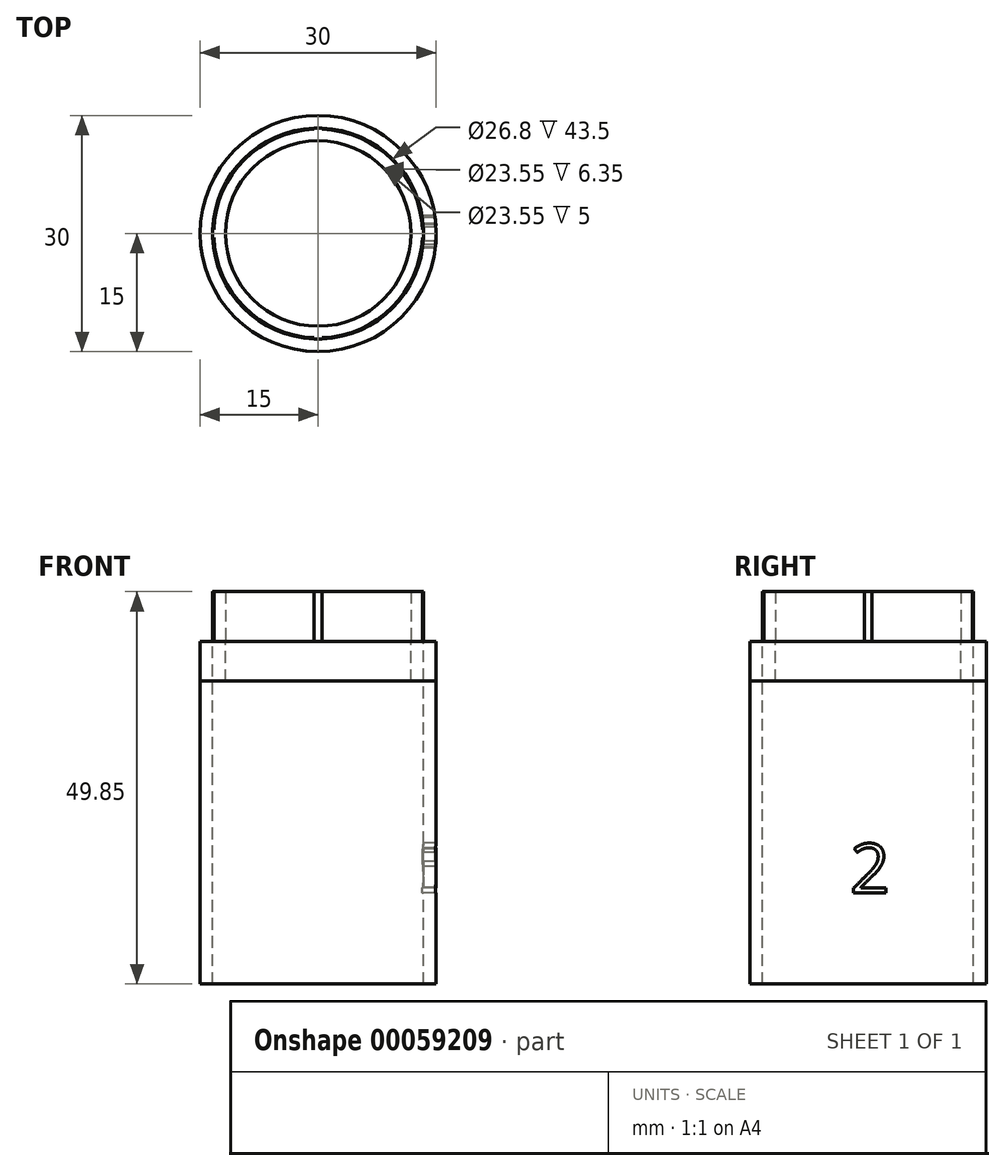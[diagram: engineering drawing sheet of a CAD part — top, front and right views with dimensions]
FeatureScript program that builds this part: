
annotation { "Feature Type Name" : "Feature", "Feature Type Description" : "" }
export const myFeature = defineFeature(function(context is Context, id is Id, definition is map)
    precondition{}
    {
        {
            var Q0;
            Q0=qCreatedBy(makeId("Top.planeOp"),FACE);
            var sketch = newSketch(context, id + "F0", { "sketchPlane" : qUnion([Q0])});
            skCircle(sketch, "E0", {"center": v(0, 0) * mm, "radius": 11.78 * mm});
            skCircle(sketch, "E1", {"center": v(0, 0) * mm, "radius": 13.25 * mm});
            skArc(sketch, "E2", {"start": v(13.4, -0.5) * mm, "mid": v(13.4, 0) * mm, "end": v(13.4, 0.5) * mm});
            skLineSegment(sketch, "E3", {"start": v(13.4, -0.5) * mm, "end": v(13.4, 0) * mm, "construction": true});
            skLineSegment(sketch, "E4", {"start": v(13.4, 0.5) * mm, "end": v(13.4, 0) * mm, "construction": true});
            skLineSegment(sketch, "E5", {"start": v(13.4, 0.5) * mm, "end": v(13.24, 0.5) * mm});
            skLineSegment(sketch, "E6", {"start": v(13.4, -0.5) * mm, "end": v(13.24, -0.5) * mm});
            skArc(sketch, "E7", {"start": v(0.5, 13.4) * mm, "mid": v(0, 13.4) * mm, "end": v(-0.5, 13.4) * mm});
            skLineSegment(sketch, "E8", {"start": v(-0.5, 13.4) * mm, "end": v(0, 13.4) * mm, "construction": true});
            skLineSegment(sketch, "E9", {"start": v(0.5, 13.4) * mm, "end": v(0, 13.4) * mm, "construction": true});
            skLineSegment(sketch, "E10", {"start": v(13.24, 0.5) * mm, "end": v(13.24, 0) * mm, "construction": true});
            skLineSegment(sketch, "E11", {"start": v(0.5, 13.4) * mm, "end": v(0.5, 13.24) * mm});
            skLineSegment(sketch, "E12", {"start": v(-0.5, 13.4) * mm, "end": v(-0.5, 13.24) * mm});
            skArc(sketch, "E13", {"start": v(-13.4, 0.5) * mm, "mid": v(-13.4, 0) * mm, "end": v(-13.4, -0.5) * mm});
            skLineSegment(sketch, "E14", {"start": v(-13.4, 0.5) * mm, "end": v(-13.4, 0) * mm, "construction": true});
            skLineSegment(sketch, "E15", {"start": v(-13.4, 0) * mm, "end": v(-13.4, -0.5) * mm, "construction": true});
            skLineSegment(sketch, "E16", {"start": v(-13.4, 0.5) * mm, "end": v(-13.24, 0.5) * mm});
            skLineSegment(sketch, "E17", {"start": v(-13.4, -0.5) * mm, "end": v(-13.24, -0.5) * mm});
            skArc(sketch, "E18", {"start": v(-0.5, -13.4) * mm, "mid": v(0, -13.4) * mm, "end": v(0.5, -13.4) * mm});
            skLineSegment(sketch, "E19", {"start": v(0.5, -13.4) * mm, "end": v(0, -13.4) * mm, "construction": true});
            skLineSegment(sketch, "E20", {"start": v(0, -13.4) * mm, "end": v(-0.5, -13.4) * mm, "construction": true});
            skLineSegment(sketch, "E21", {"start": v(0.5, -13.4) * mm, "end": v(0.5, -13.24) * mm});
            skLineSegment(sketch, "E22", {"start": v(-0.5, -13.4) * mm, "end": v(-0.5, -13.24) * mm});
            skSolve(sketch);
        }
        {
            var Q0;
            Q0=qSketchRegion(id+"F0",true);
            extrude(context, id + "F1", {"entities" : qUnion([Q0]), "depth" : 6.35 * mm});
        }
        {
            var Q0;
            Q0=qCreatedBy(makeId("Top.planeOp"),FACE);
            var sketch = newSketch(context, id + "F2", { "sketchPlane" : qUnion([Q0])});
            skCircle(sketch, "E23", {"center": v(0, 0) * mm, "radius": 13.4 * mm});
            skCircle(sketch, "E24", {"center": v(0, 0) * mm, "radius": 15 * mm});
            skSolve(sketch);
        }
        {
            var Q0;
            Q0=qSketchRegion(id+"F2",true);
            extrude(context, id + "F3", {"entities" : qUnion([Q0]), "operationType" : NewBodyOperationType.ADD, "oppositeDirection" : true, "depth" : 43.5 * mm});
        }
        {
            var Q0;
            Q0=qCreatedBy(makeId("Top.planeOp"),FACE);
            var sketch = newSketch(context, id + "F4", { "sketchPlane" : qUnion([Q0])});
            skCircle(sketch, "E25", {"center": v(0, 0) * mm, "radius": 11.78 * mm});
            skCircle(sketch, "E26", {"center": v(0, 0) * mm, "radius": 15 * mm});
            skSolve(sketch);
        }
        {
            var Q0;
            Q0=qSketchRegion(id+"F4",true);
            extrude(context, id + "F5", {"entities" : qUnion([Q0]), "oppositeDirection" : true, "depth" : 5 * mm});
        }
        {
            var Q0;
            Q0=qCreatedBy(makeId("Right.planeOp"),FACE);
            var sketch = newSketch(context, id + "F6", { "sketchPlane" : qUnion([Q0])});
            skText(sketch, "E27", { "text": "2", "fontName": "OpenSans-Regular.ttf"});
            const initialGuessF6  = {"E27": [-0.00226, -0.03192, 1, 0, 0.0063]};
            skSetInitialGuess(sketch, initialGuessF6);
            skSolve(sketch);
        }
        {
            var Q0;
            Q0=qSketchRegion(id+"F6",true);
            extrude(context, id + "F7", {"entities" : qUnion([Q0]), "operationType" : NewBodyOperationType.REMOVE, "depth" : 25 * mm});
        }
    });
